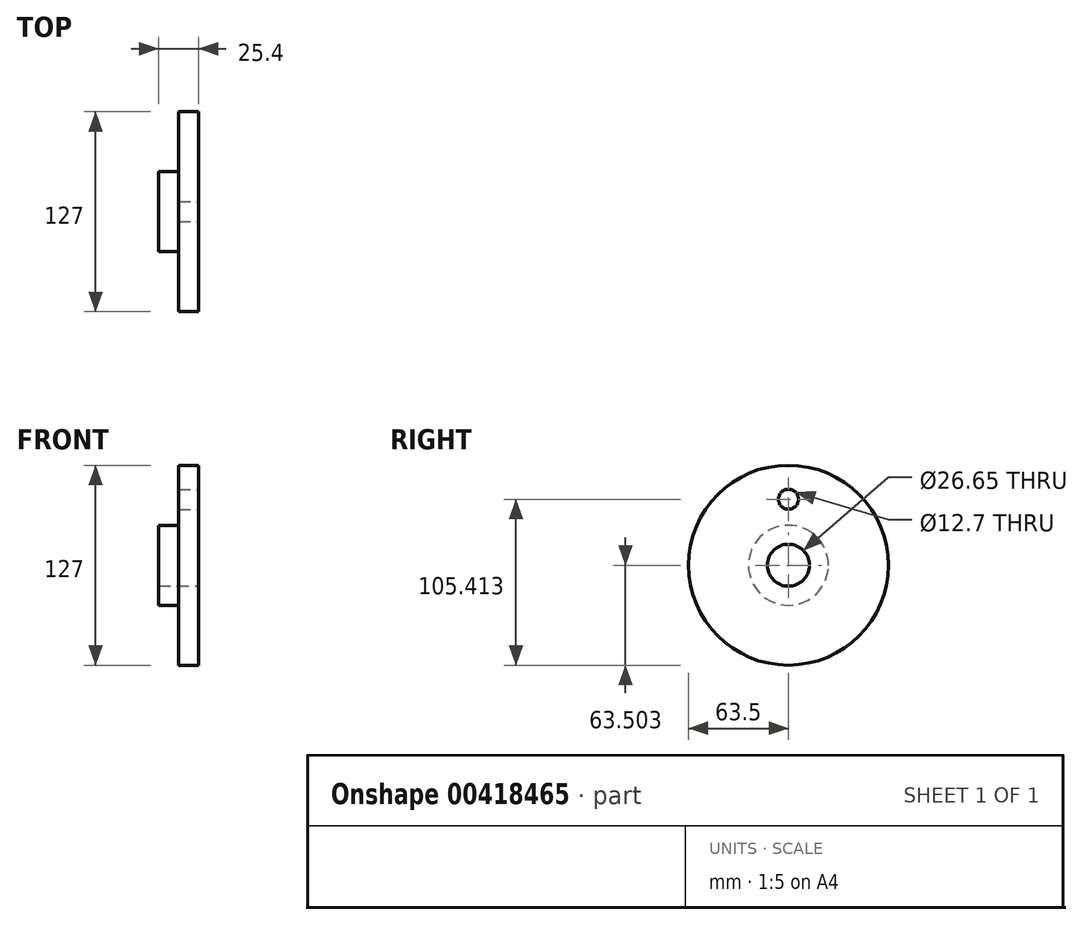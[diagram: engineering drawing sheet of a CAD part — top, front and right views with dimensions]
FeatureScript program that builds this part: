
annotation { "Feature Type Name" : "Feature", "Feature Type Description" : "" }
export const myFeature = defineFeature(function(context is Context, id is Id, definition is map)
    precondition{}
    {
        {
            var Q0;
            Q0=qCreatedBy(makeId("Front.planeOp"),FACE);
            var sketch = newSketch(context, id + "F0", { "sketchPlane" : qUnion([Q0])});
            skLineSegment(sketch, "E0", {"start": v(0, 0) * mm, "end": v(0, 50.17) * mm});
            skLineSegment(sketch, "E1", {"start": v(0, 50.17) * mm, "end": v(-12.7, 50.17) * mm});
            skLineSegment(sketch, "E2", {"start": v(-12.7, 50.17) * mm, "end": v(-12.7, 12.07) * mm});
            skLineSegment(sketch, "E3", {"start": v(-12.7, 12.07) * mm, "end": v(-25.4, 12.07) * mm});
            skLineSegment(sketch, "E4", {"start": v(-25.4, 12.07) * mm, "end": v(-25.4, 0) * mm});
            skLineSegment(sketch, "E5", {"start": v(-25.4, 0) * mm, "end": v(0, 0) * mm});
            skLineSegment(sketch, "E6", {"start": v(0, -13.33) * mm, "end": v(-25.4, -13.33) * mm, "construction": true});
            skPoint(sketch, "E7", {"position": v(-12.7, 41.91) * mm});
            skSolve(sketch);
        }
        {
            var Q0;
            Q0=makeQuery(id+"F0.imprint","IMPRINT",FACE,{"disambiguationData":[TD([[makeQuery(id+"F0.imprint","IMPRINT",EDGE,{"derivedFrom":sQuery(id+"F0.wireOp",EDGE,"E0")}),1.0]])]});
            var Q1;
            Q1=sQuery(id+"F0.wireOp",EDGE,"E6");
            revolve(context, id + "F1", {"entities" : qUnion([Q0]), "axis" : qUnion([Q1]), "revolveType" : RevolveType.FULL});
        }
        {
            var Q0;
            Q0=qCreatedBy(makeId("Right.planeOp"),FACE);
            var sketch = newSketch(context, id + "F2", { "sketchPlane" : qUnion([Q0])});
            skPoint(sketch, "E8", {"position": v(0, 28.58) * mm});
            skSolve(sketch);
        }
        {
            var Q0;
            Q0=sQuery(id+"F2.wireOp",VERTEX,"E8");
            var Q1;
            Q1=makeQuery(id+"F1.opRevolve","SWEPT_BODY",BODY,{"disambiguationData":[OSD([sQuery(id+"F0.wireOp",EDGE,"E0"),sQuery(id+"F0.wireOp",EDGE,"E1"),sQuery(id+"F0.wireOp",EDGE,"E2"),sQuery(id+"F0.wireOp",EDGE,"E3"),sQuery(id+"F0.wireOp",EDGE,"E4"),sQuery(id+"F0.wireOp",EDGE,"E5")])]});
            hole(context, id + "F3", {"style" : HoleStyle.SIMPLE, "endStyle" : HoleEndStyle.THROUGH, "holeDiameter" : 12.7 * mm, "isTappedThrough" : true, "tappedDepth" : 12.7 * mm, "tapClearance" : 3, "locations" : qUnion([Q0]), "scope" : qUnion([Q1])});
        }
    });
